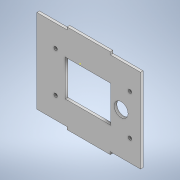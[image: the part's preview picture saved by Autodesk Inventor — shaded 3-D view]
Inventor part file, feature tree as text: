
AUTODESK INVENTOR PART (.ipt)
format: ipt  version: 2020 (Build 240168000, 168)  size: 163,328 bytes
history: native  units: in
note: dims shown in document units (in); Inventor stores cm internally (conversion verified against a paired STEP export)
features: sketch x6, extrude x4
ambient origin geometry x8: Origin, YZ Plane, XZ Plane, XY Plane, X Axis, Y Axis, Z Axis, Center Point
bodies: Solid1 (feature_tree)
feature tree (10):
  extrude  "Extrusion1"  Depth=1.9685in
  extrude  "Extrusion2"  Depth=1.378in
  extrude  "Extrusion3"  Depth=3.8189in
  extrude  "Extrusion4"  Depth=1.378in
  sketch  "Sketch6"  dims[d8=1.9685in]
  sketch  "Sketch7"  dims[d9=1.378in d10=0.1181in d11=0.0in d30=0.1575in d34=0.1575in d35=0.1575in d36=0.1575in d38=0.5512in d43=2.0039in d44=1.5748in d49=0.3937in d50=0.0in d51=0.3937in d52=0.0in d58=0.3937in d59=0.0in d12=0.1969in d13=0.0344in]
  sketch  "Sketch2"  dims[d0=0.1181in d1=1.9685in]
  sketch  "Sketch3"  dims[d2=1.378in d3=1.378in]
  sketch  "Sketch4"  dims[d4=3.8189in d5=3.8189in]
  sketch  "Sketch5"  dims[d6=0.1181in d7=1.378in]
